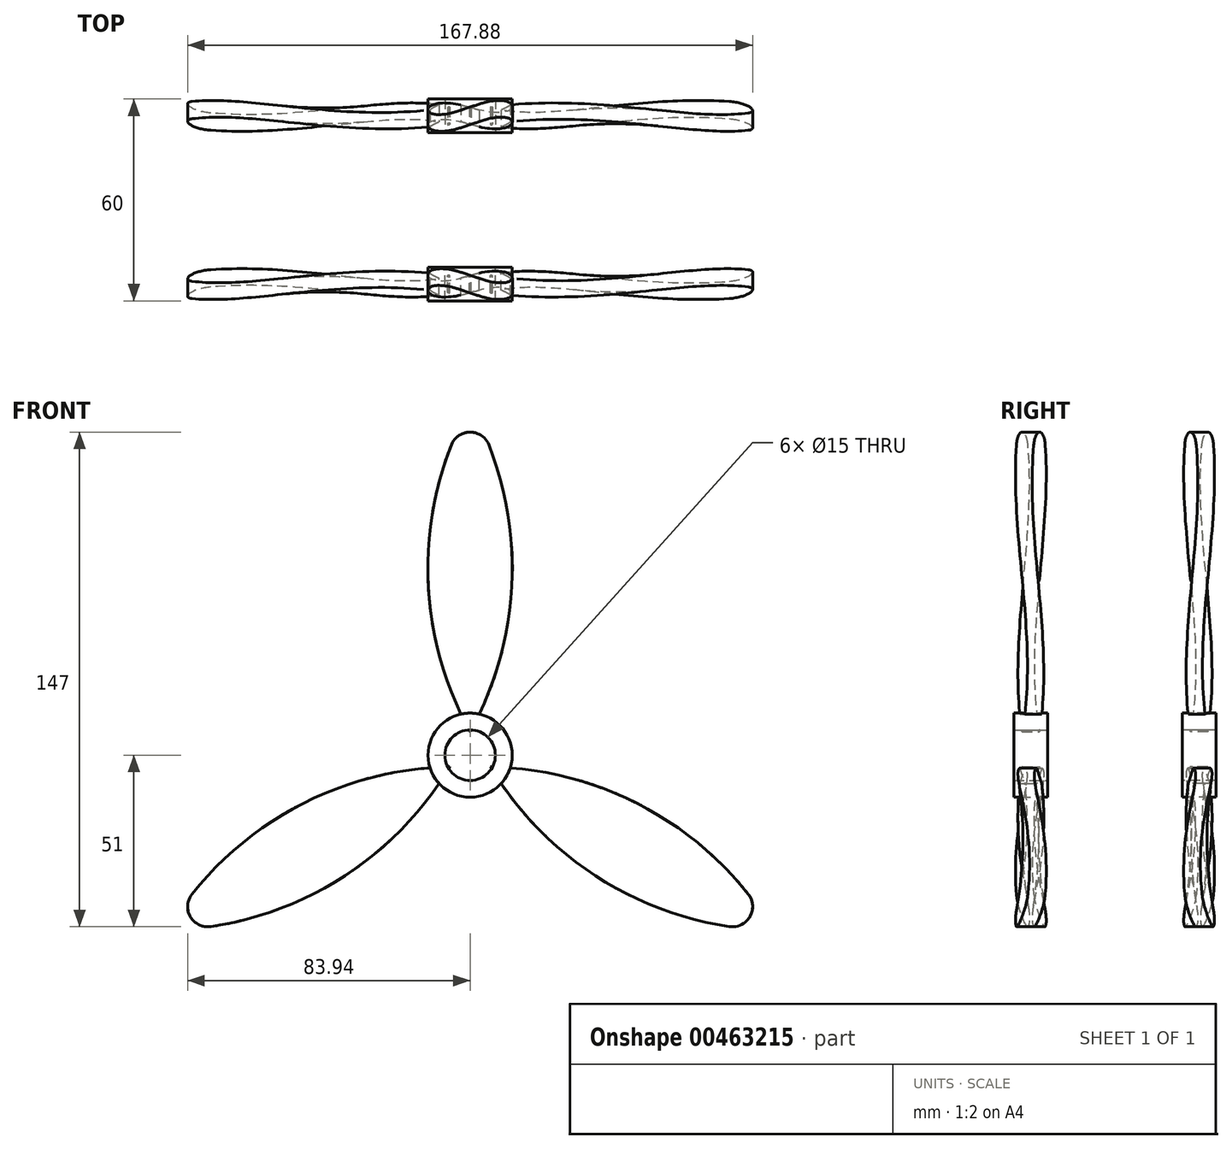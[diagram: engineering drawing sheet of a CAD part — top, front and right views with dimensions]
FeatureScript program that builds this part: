
annotation { "Feature Type Name" : "Feature", "Feature Type Description" : "" }
export const myFeature = defineFeature(function(context is Context, id is Id, definition is map)
    precondition{}
    {
        {
            var Q0;
            Q0=qCreatedBy(makeId("Top.planeOp"),FACE);
            cPlane(context, id + "F0", {"entities" : qUnion([Q0]), "cplaneType" : CPlaneType.OFFSET, "offset" : 100 * mm, "width" : 150 * mm, "height" : 150 * mm});
        }
        {
            var Q0;
            Q0=qCreatedBy(makeId("Top.planeOp"),FACE);
            var sketch = newSketch(context, id + "F1", { "sketchPlane" : qUnion([Q0])});
            skLineSegment(sketch, "E0", {"start": v(-24.35, -6.2) * mm, "end": v(22.64, 10.9) * mm});
            skLineSegment(sketch, "E1", {"start": v(-24.35, -6.2) * mm, "end": v(-22.64, -10.9) * mm});
            skLineSegment(sketch, "E2", {"start": v(24.35, 6.2) * mm, "end": v(-22.64, -10.9) * mm});
            skLineSegment(sketch, "E3", {"start": v(24.35, 6.2) * mm, "end": v(22.64, 10.9) * mm});
            skLineSegment(sketch, "E4", {"start": v(0, 32.62) * mm, "end": v(0, -34.09) * mm, "construction": true});
            skLineSegment(sketch, "E5", {"start": v(-32.92, 0) * mm, "end": v(42.76, 0) * mm, "construction": true});
            skLineSegment(sketch, "E6", {"start": v(23.5, 8.55) * mm, "end": v(-23.5, -8.55) * mm, "construction": true});
            skLineSegment(sketch, "E7", {"start": v(-0.86, 2.35) * mm, "end": v(0.86, -2.35) * mm, "construction": true});
            skSolve(sketch);
        }
        {
            var Q0;
            Q0=qCreatedBy(id+"F0.planeOp",FACE);
            var sketch = newSketch(context, id + "F2", { "sketchPlane" : qUnion([Q0])});
            skLineSegment(sketch, "E8", {"start": v(0, 23.29) * mm, "end": v(0, -21.04) * mm, "construction": true});
            skLineSegment(sketch, "E9", {"start": v(-22.67, 0) * mm, "end": v(29.77, 0) * mm, "construction": true});
            skLineSegment(sketch, "E10", {"start": v(-22.64, 10.9) * mm, "end": v(24.35, -6.2) * mm});
            skLineSegment(sketch, "E11", {"start": v(24.35, -6.2) * mm, "end": v(22.64, -10.9) * mm});
            skLineSegment(sketch, "E12", {"start": v(22.64, -10.9) * mm, "end": v(-24.35, 6.2) * mm});
            skLineSegment(sketch, "E13", {"start": v(-24.35, 6.2) * mm, "end": v(-22.64, 10.9) * mm});
            skLineSegment(sketch, "E14", {"start": v(-23.5, 8.55) * mm, "end": v(23.5, -8.55) * mm, "construction": true});
            skLineSegment(sketch, "E15", {"start": v(0.86, 2.35) * mm, "end": v(-0.86, -2.35) * mm, "construction": true});
            skSolve(sketch);
        }
        {
            var Q0;
            Q0=makeQuery(id+"F1.imprint","IMPRINT",FACE,{"disambiguationData":[TD([[makeQuery(id+"F1.imprint","IMPRINT",EDGE,{"derivedFrom":sQuery(id+"F1.wireOp",EDGE,"E0")}),-1.0]])]});
            var Q1;
            Q1=makeQuery(id+"F2.imprint","IMPRINT",FACE,{"disambiguationData":[TD([[makeQuery(id+"F2.imprint","IMPRINT",EDGE,{"derivedFrom":sQuery(id+"F2.wireOp",EDGE,"E10")}),-1.0]])]});
            loft(context, id + "F3", {"sheetProfilesArray" : [{ "sheetProfileEntities" : qUnion([Q0]) }, { "sheetProfileEntities" : qUnion([Q1]) }]});
        }
        {
            var Q0;
            Q0=qCreatedBy(makeId("Front.planeOp"),FACE);
            var sketch = newSketch(context, id + "F4", { "sketchPlane" : qUnion([Q0])});
            skLineSegment(sketch, "E16", {"start": v(0, 0) * mm, "end": v(0, 118.85) * mm, "construction": true});
            skArc(sketch, "E17", {"start": v(0, 7) * mm, "mid": v(12.34, 48.98) * mm, "end": v(5.58, 92.2) * mm});
            skArc(sketch, "E18", {"start": v(5.58, 92.2) * mm, "mid": v(3.38, 94.96) * mm, "end": v(0, 96) * mm});
            skArc(sketch, "E19.MirrorCS", {"start": v(0, 7) * mm, "mid": v(-12.34, 48.98) * mm, "end": v(-5.58, 92.2) * mm});
            skArc(sketch, "E20.MirrorCS", {"start": v(-5.58, 92.2) * mm, "mid": v(-3.38, 94.96) * mm, "end": v(0, 96) * mm});
            skSolve(sketch);
        }
        {
            var Q0;
            Q0 = qSketchRegion(id + "F4", true);
            extrude(context, id + "F5", {"entities" : qUnion([Q0]), "operationType" : NewBodyOperationType.INTERSECT, "endBound" : BoundingType.SYMMETRIC, "depth" : 20 * mm});
        }
        {
            var Q0;
            Q0=qCreatedBy(makeId("Front.planeOp"),FACE);
            var sketch = newSketch(context, id + "F6", { "sketchPlane" : qUnion([Q0])});
            skCircle(sketch, "E21", {"center": v(0, 0) * mm, "radius": 12.5 * mm});
            skCircle(sketch, "E22", {"center": v(0, 0) * mm, "radius": 7.5 * mm});
            skSolve(sketch);
        }
        {
            var Q0;
            Q0 = qSketchRegion(id + "F6", true);
            extrude(context, id + "F7", {"entities" : qUnion([Q0]), "operationType" : NewBodyOperationType.ADD, "endBound" : BoundingType.SYMMETRIC, "depth" : 10 * mm});
        }
        {
            var Q0;
            Q0=makeQuery(id+"F3.opLoft","SWEPT_BODY",BODY,{"disambiguationData":[OSD([makeQuery(id+"F1.imprint","IMPRINT",FACE,{"disambiguationData":[TD([[makeQuery(id+"F1.imprint","IMPRINT",EDGE,{"derivedFrom":sQuery(id+"F1.wireOp",EDGE,"E0")}),-1.0]])]}),makeQuery(id+"F2.imprint","IMPRINT",FACE,{"disambiguationData":[TD([[makeQuery(id+"F2.imprint","IMPRINT",EDGE,{"derivedFrom":sQuery(id+"F2.wireOp",EDGE,"E10")}),-1.0]])]})])]});
            var Q1;
            Q1=makeQuery(id+"F7.opExtrude","SWEPT_FACE",FACE,{"disambiguationData":[OSD([sQuery(id+"F6.wireOp",EDGE,"E21")])]});
            circularPattern(context, id + "F8", {"entities" : qUnion([Q0]), "axis" : qUnion([Q1]), "angle" : 360 * degree, "instanceCount" : 3, "equalSpace" : true});
        }
        {
            var Q0;
            Q0=qCreatedBy(makeId("Front.planeOp"),FACE);
            cPlane(context, id + "F9", {"entities" : qUnion([Q0]), "cplaneType" : CPlaneType.OFFSET, "offset" : 25 * mm, "oppositeDirection" : true, "width" : 150 * mm, "height" : 150 * mm});
        }
        {
            var Q0;
            Q0=makeQuery(id+"F3.opLoft","SWEPT_BODY",BODY,{"disambiguationData":[OSD([makeQuery(id+"F1.imprint","IMPRINT",FACE,{"disambiguationData":[TD([[makeQuery(id+"F1.imprint","IMPRINT",EDGE,{"derivedFrom":sQuery(id+"F1.wireOp",EDGE,"E0")}),-1.0]])]}),makeQuery(id+"F2.imprint","IMPRINT",FACE,{"disambiguationData":[TD([[makeQuery(id+"F2.imprint","IMPRINT",EDGE,{"derivedFrom":sQuery(id+"F2.wireOp",EDGE,"E10")}),-1.0]])]})])]});
            var Q1;
            Q1=makeQuery(id+"F8.opPattern","COPY",BODY,{"derivedFrom":makeQuery(id+"F3.opLoft","SWEPT_BODY",BODY,{"disambiguationData":[OSD([makeQuery(id+"F1.imprint","IMPRINT",FACE,{"disambiguationData":[TD([[makeQuery(id+"F1.imprint","IMPRINT",EDGE,{"derivedFrom":sQuery(id+"F1.wireOp",EDGE,"E0")}),-1.0]])]}),makeQuery(id+"F2.imprint","IMPRINT",FACE,{"disambiguationData":[TD([[makeQuery(id+"F2.imprint","IMPRINT",EDGE,{"derivedFrom":sQuery(id+"F2.wireOp",EDGE,"E10")}),-1.0]])]})])]}),"instanceName":"2"});
            var Q2;
            Q2=makeQuery(id+"F8.opPattern","COPY",BODY,{"derivedFrom":makeQuery(id+"F3.opLoft","SWEPT_BODY",BODY,{"disambiguationData":[OSD([makeQuery(id+"F1.imprint","IMPRINT",FACE,{"disambiguationData":[TD([[makeQuery(id+"F1.imprint","IMPRINT",EDGE,{"derivedFrom":sQuery(id+"F1.wireOp",EDGE,"E0")}),-1.0]])]}),makeQuery(id+"F2.imprint","IMPRINT",FACE,{"disambiguationData":[TD([[makeQuery(id+"F2.imprint","IMPRINT",EDGE,{"derivedFrom":sQuery(id+"F2.wireOp",EDGE,"E10")}),-1.0]])]})])]}),"instanceName":"1"});
            var Q3;
            Q3=qCreatedBy(id+"F9.planeOp",FACE);
            mirror(context, id + "F10", {"entities" : qUnion([Q0, Q1, Q2]), "mirrorPlane" : qUnion([Q3])});
        }
    });
